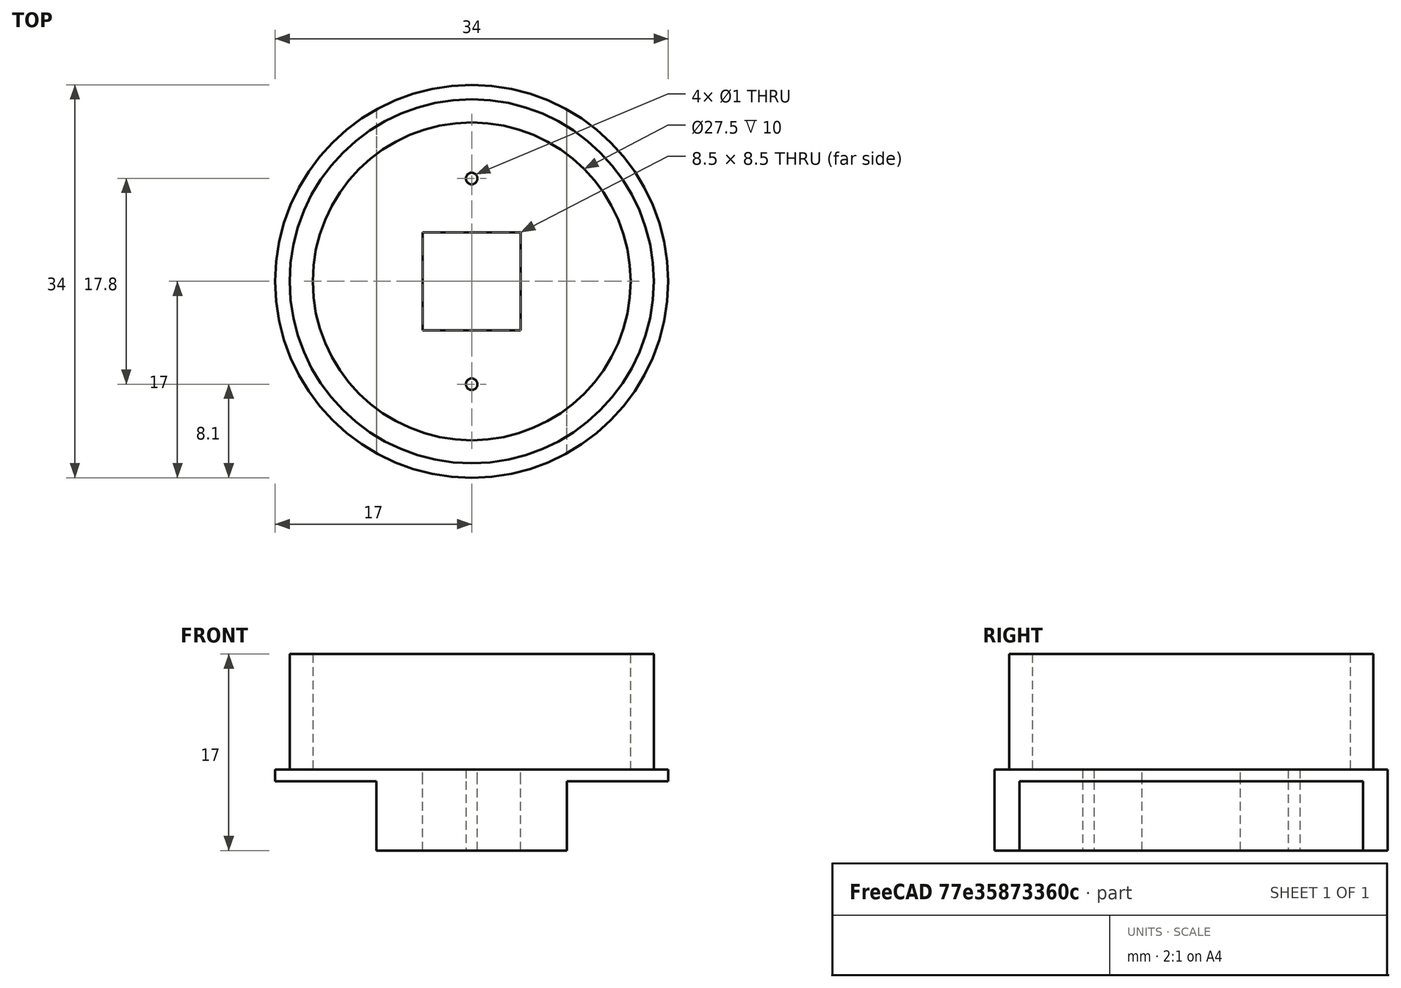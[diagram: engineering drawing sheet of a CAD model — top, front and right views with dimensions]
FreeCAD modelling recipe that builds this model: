
FCSTD DOCUMENT  (FreeCAD 0.20R29177 +426 (Git))
Label: Logitech.C270
License: All rights reserved
LicenseURL: http://en.wikipedia.org/wiki/All_rights_reserved
objects: Part::Part2DObjectPython×11, Part::Cut×10, Part::Extrusion×9, Part::Cylinder×3, Part::MultiFuse×1
note: 34 computed .brp shape members not serialized (recipe doc carries the construction recipe); baked Part::Feature solids carry a one-line shape summary decoded from their .brp

FEATURE [Part::Cylinder] Cylinder
  Angle = 360
  AttacherType = Attacher::AttachEngine3D
  FirstAngle = 0
  Height = 10
  Radius = 15.75
  SecondAngle = 0
FEATURE [Part::Cylinder] Cylinder001
  Angle = 360
  AttacherType = Attacher::AttachEngine3D
  FirstAngle = 0
  Height = 10
  Radius = 13.75
  SecondAngle = 0
FEATURE [Part::Cut] Cut
  Base = -> Cylinder
  Tool = -> Cylinder001
FEATURE [Part::Cylinder] Cylinder002
  Angle = 360
  AttacherType = Attacher::AttachEngine3D
  FirstAngle = 0
  Height = 1
  Placement = pos=(0,0,-1) rot=(0,0,1;0rad)
  Radius = 15.75
  SecondAngle = 0
FEATURE [Part::Part2DObjectPython] Circle  # Draft 2D object (typed FeaturePython)
  Area = 0.785398
  FirstAngle = 0
  LastAngle = 0
  MakeFace = true
  Placement = pos=(4e-15,-8.9,-1) rot=(1,0,0;3.14159rad)
  Radius = 0.5
FEATURE [Part::Part2DObjectPython] Circle001  # Draft 2D object (typed FeaturePython)
  Area = 0.785398
  FirstAngle = 0
  LastAngle = 0
  MakeFace = true
  Placement = pos=(4e-15,8.9,-1) rot=(1,0,0;3.14159rad)
  Radius = 0.5
FEATURE [Part::Extrusion] Extrusion
  Base = -> Circle
  Dir = (0,0,22.6601)
  DirMode = 0
  FaceMakerClass = Part::FaceMakerBullseye
  LengthFwd = 0
  LengthRev = 0
  Solid = true
  Symmetric = false
FEATURE [Part::Extrusion] Extrusion001
  Base = -> Circle001
  Dir = (0,0,25.4118)
  DirMode = 0
  FaceMakerClass = Part::FaceMakerBullseye
  LengthFwd = 0
  LengthRev = 0
  Solid = true
  Symmetric = false
FEATURE [Part::Cut] Cut001
  Base = -> Cylinder002
  Tool = -> Extrusion001
FEATURE [Part::Cut] Cut002
  Base = -> Cut001
  Tool = -> Extrusion
FEATURE [Part::Part2DObjectPython] Rectangle  # Draft 2D object (typed FeaturePython)
  Area = 72.25
  ChamferSize = 0
  Columns = 1
  FilletRadius = 0
  Height = 8.5
  Length = 8.5
  MakeFace = true
  Placement = pos=(-4.25,4.25,-1) rot=(1,0,0;3.14159rad)
  Rows = 1
FEATURE [Part::Extrusion] Extrusion002
  Base = -> Rectangle
  Dir = (0,0,28.5447)
  DirMode = 0
  FaceMakerClass = Part::FaceMakerBullseye
  LengthFwd = 0
  LengthRev = 0
  Solid = true
  Symmetric = false
FEATURE [Part::Cut] Cut003
  Base = -> Cut002
  Tool = -> Extrusion002
FEATURE [Part::Part2DObjectPython] Circle005  # Draft 2D object (typed FeaturePython)
  Area = 907.92
  FirstAngle = 0
  LastAngle = 0
  MakeFace = true
  Placement = pos=(0,-1e-15,-1) rot=(1,0,0;3.14159rad)
  Radius = 17
FEATURE [Part::Extrusion] Extrusion007
  Base = -> Circle005
  Dir = (0,0,1)
  DirMode = 0
  FaceMakerClass = Part::FaceMakerBullseye
  LengthFwd = 0
  LengthRev = 0
  Solid = true
  Symmetric = false
FEATURE [Part::Part2DObjectPython] Circle006  # Draft 2D object (typed FeaturePython)
  Area = 593.957
  FirstAngle = 0
  LastAngle = 0
  MakeFace = true
  Placement = pos=(-8.9e-15,-7e-15,10) rot=(0,0,1;0rad)
  Radius = 13.75
FEATURE [Part::Extrusion] Extrusion008
  Base = -> Circle006
  Dir = (0,0,-34.5801)
  DirMode = 0
  FaceMakerClass = Part::FaceMakerBullseye
  LengthFwd = 0
  LengthRev = 0
  Solid = true
  Symmetric = false
FEATURE [Part::Cut] Cut009
  Base = -> Extrusion007
  Tool = -> Extrusion008
FEATURE [Part::Part2DObjectPython] Circle007  # Draft 2D object (typed FeaturePython)
  Area = 907.92
  FirstAngle = 0
  LastAngle = 0
  MakeFace = true
  Placement = pos=(-5e-15,-4e-15,-7) rot=(1,0,0;3.14159rad)
  Radius = 17
FEATURE [Part::Part2DObjectPython] Rectangle004  # Draft 2D object (typed FeaturePython)
  Area = 1570.36
  ChamferSize = 0
  Columns = 1
  FilletRadius = 0
  Height = 60.9789
  Length = 25.7525
  MakeFace = true
  Placement = pos=(-34.0025,33.56,-7) rot=(1,0,0;3.14159rad)
  Rows = 1
FEATURE [Part::Part2DObjectPython] Rectangle005  # Draft 2D object (typed FeaturePython)
  Area = 2516.67
  ChamferSize = 0
  Columns = 1
  FilletRadius = 0
  Height = 95.4755
  Length = 26.3593
  MakeFace = true
  Placement = pos=(8.25,33.56,-7) rot=(1,0,0;3.14159rad)
  Rows = 1
FEATURE [Part::Cut] Cut010
  Base = -> Circle007
  Tool = -> Rectangle005
FEATURE [Part::Cut] Cut011
  Base = -> Cut010
  Tool = -> Rectangle004
FEATURE [Part::Part2DObjectPython] Circle008  # Draft 2D object (typed FeaturePython)
  Area = 0.785398
  FirstAngle = 0
  LastAngle = 0
  MakeFace = true
  Placement = pos=(4e-15,-8.9,-7) rot=(1,0,0;3.14159rad)
  Radius = 0.5
FEATURE [Part::Part2DObjectPython] Circle009  # Draft 2D object (typed FeaturePython)
  Area = 0.785398
  FirstAngle = 0
  LastAngle = 0
  MakeFace = true
  Placement = pos=(4e-15,8.9,-7) rot=(1,0,0;3.14159rad)
  Radius = 0.5
FEATURE [Part::Part2DObjectPython] Rectangle006  # Draft 2D object (typed FeaturePython)
  Area = 72.25
  ChamferSize = 0
  Columns = 1
  FilletRadius = 0
  Height = 8.5
  Length = 8.5
  MakeFace = true
  Placement = pos=(-4.25,4.25,-7) rot=(1,0,0;3.14159rad)
  Rows = 1
FEATURE [Part::Extrusion] Extrusion009
  Base = -> Cut011
  Dir = (0,0,6)
  DirMode = 0
  FaceMakerClass = Part::FaceMakerBullseye
  LengthFwd = 0
  LengthRev = 0
  Solid = true
  Symmetric = false
FEATURE [Part::Extrusion] Extrusion010
  Base = -> Rectangle006
  Dir = (0,0,47.9774)
  DirMode = 0
  FaceMakerClass = Part::FaceMakerBullseye
  LengthFwd = 0
  LengthRev = 0
  Solid = true
  Symmetric = false
FEATURE [Part::Extrusion] Extrusion011
  Base = -> Circle008
  Dir = (0,0,25.9852)
  DirMode = 0
  FaceMakerClass = Part::FaceMakerBullseye
  LengthFwd = 0
  LengthRev = 0
  Solid = true
  Symmetric = false
FEATURE [Part::Extrusion] Extrusion012
  Base = -> Circle009
  Dir = (0,0,43.3804)
  DirMode = 0
  FaceMakerClass = Part::FaceMakerBullseye
  LengthFwd = 0
  LengthRev = 0
  Solid = true
  Symmetric = false
FEATURE [Part::Cut] Cut012
  Base = -> Extrusion009
  Tool = -> Extrusion012
FEATURE [Part::Cut] Cut013
  Base = -> Cut012
  Tool = -> Extrusion011
FEATURE [Part::Cut] Cut014
  Base = -> Cut013
  Tool = -> Extrusion010
FEATURE [Part::MultiFuse] Fusion
  Shapes = -> [Cut014,Cut009,Cut003,Cut]
